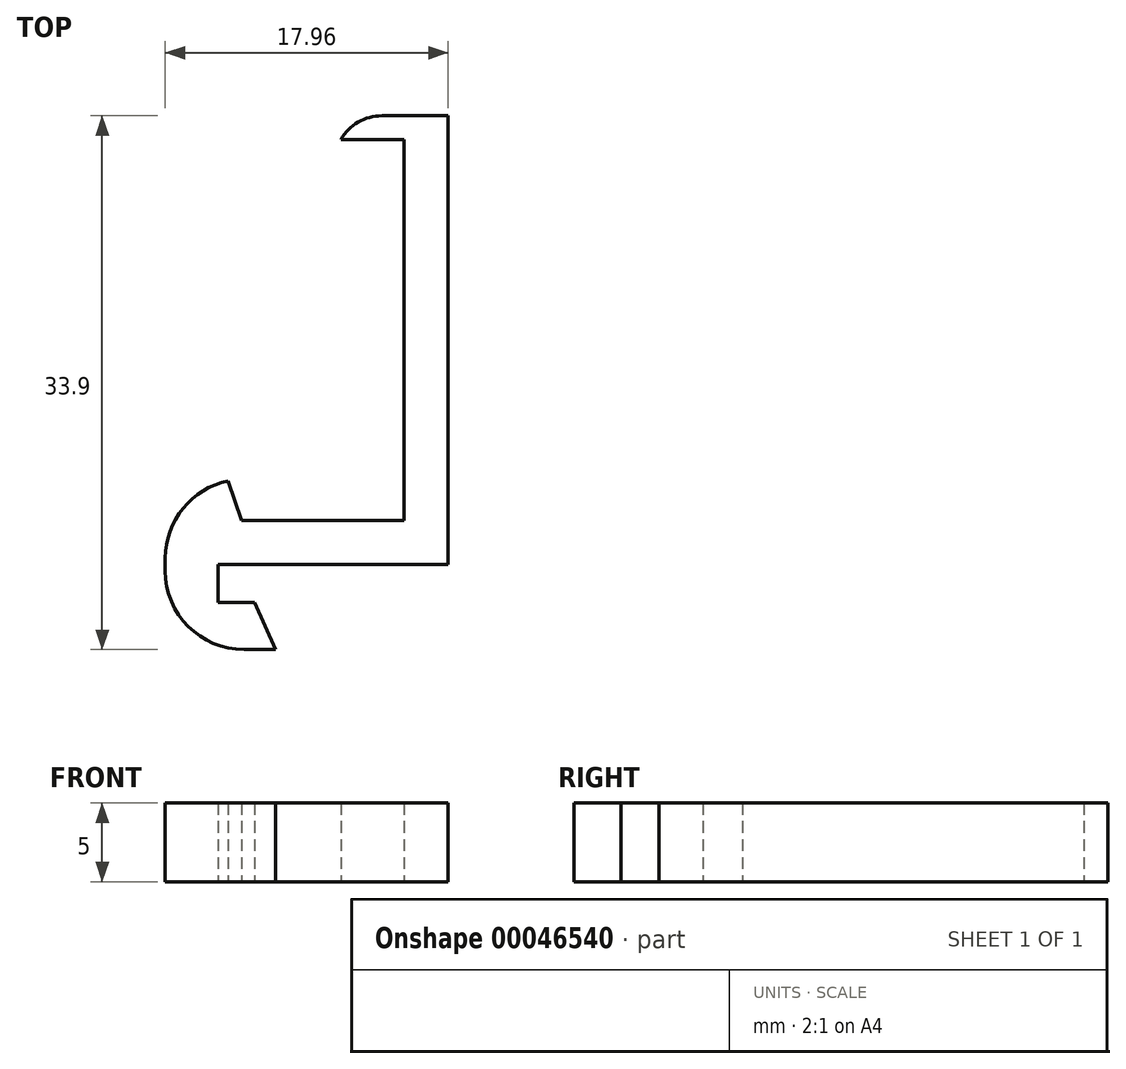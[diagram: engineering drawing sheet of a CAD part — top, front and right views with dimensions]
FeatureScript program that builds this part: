
annotation { "Feature Type Name" : "Feature", "Feature Type Description" : "" }
export const myFeature = defineFeature(function(context is Context, id is Id, definition is map)
    precondition{}
    {
        {
            var Q0;
            Q0=qCreatedBy(makeId("Top.planeOp"),FACE);
            var sketch = newSketch(context, id + "F0", { "sketchPlane" : qUnion([Q0])});
            skLineSegment(sketch, "E0", {"start": v(-10.56, -5.5) * mm, "end": v(-17.56, -5.5) * mm});
            skLineSegment(sketch, "E1", {"start": v(-17.56, -5.5) * mm, "end": v(-17.56, 5.2) * mm});
            skLineSegment(sketch, "E2", {"start": v(-17.56, 5.2) * mm, "end": v(-13.56, 5.2) * mm});
            skLineSegment(sketch, "E3", {"start": v(-13.56, 5.2) * mm, "end": v(-12.7, 2.7) * mm});
            skLineSegment(sketch, "E4", {"start": v(-12.7, 2.7) * mm, "end": v(-2.4, 2.7) * mm});
            skLineSegment(sketch, "E5", {"start": v(-2.4, 2.7) * mm, "end": v(-2.4, 26.9) * mm});
            skLineSegment(sketch, "E6", {"start": v(-2.4, 26.9) * mm, "end": v(-6.4, 26.9) * mm});
            skLineSegment(sketch, "E7", {"start": v(0, 28.4) * mm, "end": v(0, 0) * mm});
            skLineSegment(sketch, "E8", {"start": v(0, 0) * mm, "end": v(-14.2, 0) * mm});
            skLineSegment(sketch, "E9", {"start": v(-14.2, 0) * mm, "end": v(-14.2, -2.5) * mm});
            skLineSegment(sketch, "E10", {"start": v(-14.2, -2.5) * mm, "end": v(-11.88, -2.5) * mm});
            skLineSegment(sketch, "E11", {"start": v(-11.88, -2.5) * mm, "end": v(-10.56, -5.5) * mm});
            skLineSegment(sketch, "E12", {"start": v(-6.4, 28.4) * mm, "end": v(0, 28.4) * mm});
            skLineSegment(sketch, "E13", {"start": v(-6.4, 28.4) * mm, "end": v(-6.4, 26.9) * mm});
            skLineSegment(sketch, "E14", {"start": v(0, 28.4) * mm, "end": v(0.4, 28.4) * mm});
            skLineSegment(sketch, "E15", {"start": v(0.4, 28.4) * mm, "end": v(0.4, 0) * mm});
            skLineSegment(sketch, "E16", {"start": v(0.4, 0) * mm, "end": v(0, 0) * mm});
            skLineSegment(sketch, "E17", {"start": v(-14.2, -0.1) * mm, "end": v(0.4, -0.1) * mm});
            skLineSegment(sketch, "E18", {"start": v(0.4, -0.1) * mm, "end": v(0.4, 0) * mm});
            skSolve(sketch);
        }
        {
            var Q0;
            Q0=qSketchRegion(id+"F0",true);
            extrude(context, id + "F1", {"entities" : qUnion([Q0]), "depth" : 5 * mm});
        }
        {
            var Q0;
            Q0=makeQuery(id+"F1.opExtrude","SWEPT_EDGE",EDGE,{"disambiguationData":[OSD([sQuery(id+"F0.wireOp",EDGE,"E12"),sQuery(id+"F0.wireOp",EDGE,"E13")])]});
            fillet(context, id + "F2", {"entities" : qUnion([Q0]), "radius" : 3 * mm, "tangentPropagation" : true, "allowEdgeOverflow" : false});
        }
        {
            var Q0;
            Q0=makeQuery(id+"F1.opExtrude","SWEPT_EDGE",EDGE,{"disambiguationData":[OSD([sQuery(id+"F0.wireOp",EDGE,"E1"),sQuery(id+"F0.wireOp",EDGE,"E2")])]});
            var Q1;
            Q1=makeQuery(id+"F1.opExtrude","SWEPT_EDGE",EDGE,{"disambiguationData":[OSD([sQuery(id+"F0.wireOp",EDGE,"E0"),sQuery(id+"F0.wireOp",EDGE,"E1")])]});
            fillet(context, id + "F3", {"entities" : qUnion([Q0, Q1]), "radius" : 5 * mm, "tangentPropagation" : true, "allowEdgeOverflow" : false});
        }
    });
